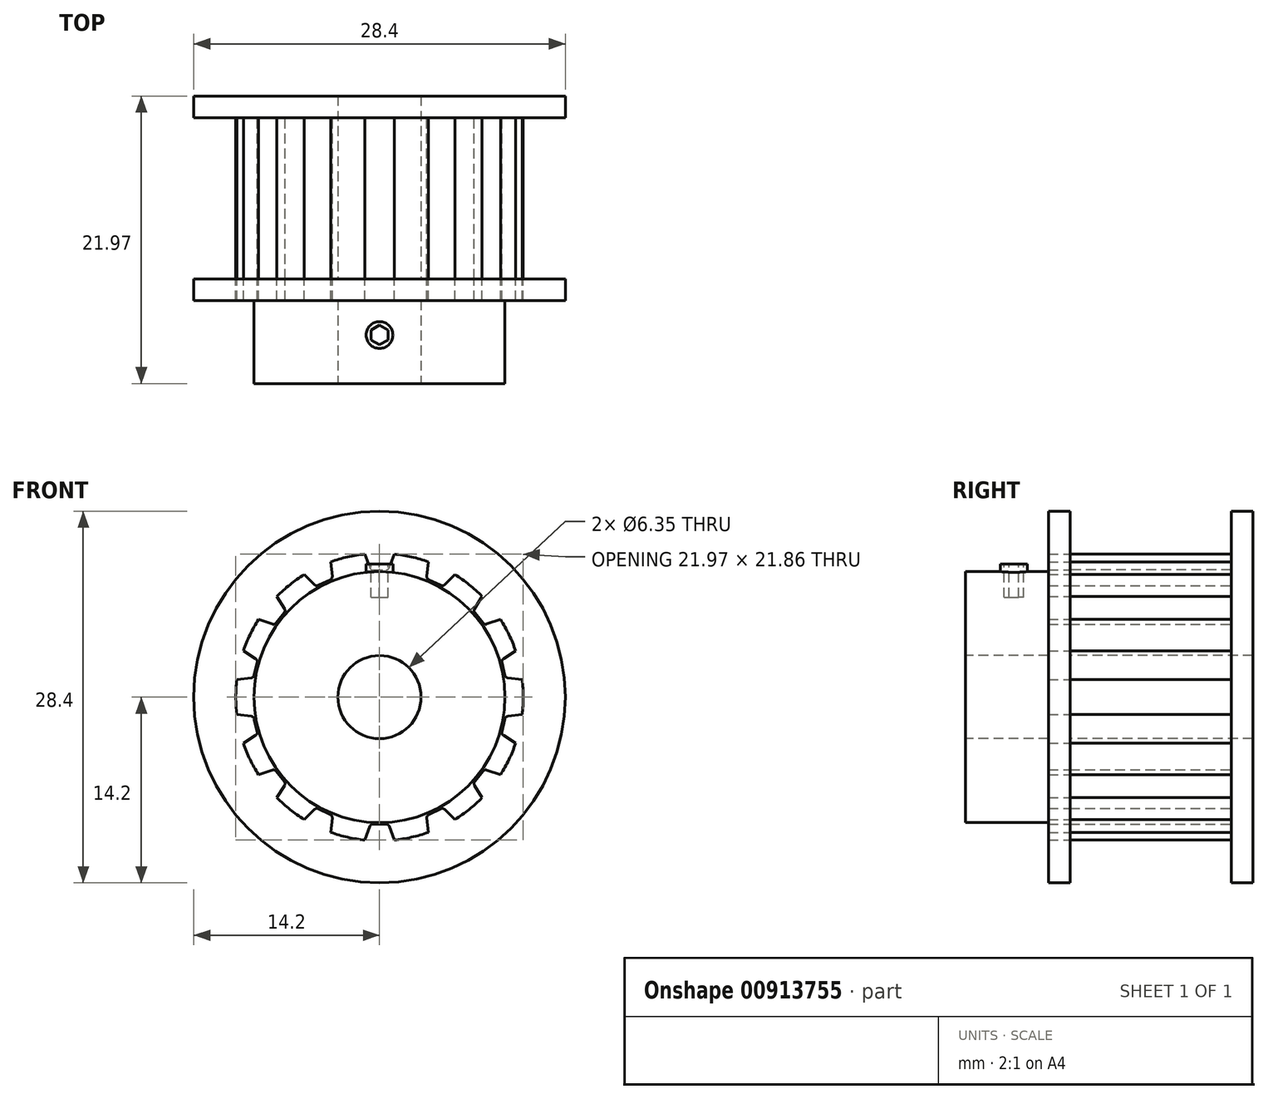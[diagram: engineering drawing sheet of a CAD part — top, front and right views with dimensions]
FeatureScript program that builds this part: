
annotation { "Feature Type Name" : "Feature", "Feature Type Description" : "" }
export const myFeature = defineFeature(function(context is Context, id is Id, definition is map)
    precondition{}
    {
        {
            var Q0;
            Q0=qCreatedBy(makeId("Front.planeOp"),FACE);
            var sketch = newSketch(context, id + "F0", { "sketchPlane" : qUnion([Q0])});
            skCircle(sketch, "E0", {"center": v(0, 0) * mm, "radius": 10.99 * mm});
            skSolve(sketch);
        }
        {
            var Q0;
            Q0=qSketchRegion(id+"F0",true);
            extrude(context, id + "F1", {"entities" : qUnion([Q0]), "depth" : 12.32 * mm});
        }
        {
            var Q0;
            Q0=makeQuery(id+"F1.opExtrude","CAP_FACE",FACE,{"disambiguationData":[OSD([sQuery(id+"F0.wireOp",EDGE,"E0")])],"isStart":false});
            var sketch = newSketch(context, id + "F2", { "sketchPlane" : qUnion([Q0])});
            skLineSegment(sketch, "E1", {"start": v(-1.13, 10.93) * mm, "end": v(-0.69, 9.72) * mm});
            skLineSegment(sketch, "E2", {"start": v(-0.69, 9.72) * mm, "end": v(0.69, 9.72) * mm});
            skLineSegment(sketch, "E3", {"start": v(0.69, 9.72) * mm, "end": v(1.13, 10.93) * mm});
            skLineSegment(sketch, "E4", {"start": v(0, 12.07) * mm, "end": v(0, 0) * mm, "construction": true});
            skArc(sketch, "E5", {"start": v(1.13, 10.93) * mm, "mid": v(0, 10.99) * mm, "end": v(-1.13, 10.93) * mm});
            skSolve(sketch);
        }
        {
            var Q0;
            Q0=qSketchRegion(id+"F2",true);
            extrude(context, id + "F3", {"entities" : qUnion([Q0]), "operationType" : NewBodyOperationType.REMOVE, "oppositeDirection" : true, "depth" : 25.4 * mm});
        }
        {
            var Q0;
            Q0=makeQuery(id+"F3.boolean.opBoolean","COPY",EDGE,{"derivedFrom":makeQuery(id+"F3.opExtrude","SWEPT_EDGE",EDGE,{"disambiguationData":[OSD([sQuery(id+"F0.wireOp",EDGE,"E0"),sQuery(id+"F2.wireOp",EDGE,"E1"),sQuery(id+"F2.wireOp",EDGE,"E5")])]})});
            var Q1;
            Q1=makeQuery(id+"F3.boolean.opBoolean","COPY",EDGE,{"derivedFrom":makeQuery(id+"F3.opExtrude","SWEPT_EDGE",EDGE,{"disambiguationData":[OSD([sQuery(id+"F0.wireOp",EDGE,"E0"),sQuery(id+"F2.wireOp",EDGE,"E3"),sQuery(id+"F2.wireOp",EDGE,"E5")])]})});
            var Q2;
            Q2=makeQuery(id+"F3.boolean.opBoolean","COPY",EDGE,{"derivedFrom":makeQuery(id+"F3.opExtrude","SWEPT_EDGE",EDGE,{"disambiguationData":[OSD([sQuery(id+"F2.wireOp",EDGE,"E1"),sQuery(id+"F2.wireOp",EDGE,"E2")])]})});
            var Q3;
            Q3=makeQuery(id+"F3.boolean.opBoolean","COPY",EDGE,{"derivedFrom":makeQuery(id+"F3.opExtrude","SWEPT_EDGE",EDGE,{"disambiguationData":[OSD([sQuery(id+"F2.wireOp",EDGE,"E2"),sQuery(id+"F2.wireOp",EDGE,"E3")])]})});
            fillet(context, id + "F4", {"entities" : qUnion([Q0, Q1, Q2, Q3]), "radius" : 0.25 * mm, "tangentPropagation" : true, "allowEdgeOverflow" : false});
        }
        {
            var Q0;
            Q0=qCreatedBy(makeId("Right.planeOp"),FACE);
            var sketch = newSketch(context, id + "F5", { "sketchPlane" : qUnion([Q0])});
            skLineSegment(sketch, "E6", {"start": v(-15.42, 0) * mm, "end": v(11.48, 0) * mm, "construction": true});
            skSolve(sketch);
        }
        {
            var Q0;
            Q0=makeQuery(id+"F3.boolean.opBoolean","COPY",FACE,{"derivedFrom":makeQuery(id+"F3.opExtrude","SWEPT_FACE",FACE,{"disambiguationData":[OSD([sQuery(id+"F2.wireOp",EDGE,"E1")])]})});
            var Q1;
            Q1=makeQuery(id+"F3.boolean.opBoolean","COPY",FACE,{"derivedFrom":makeQuery(id+"F3.opExtrude","SWEPT_FACE",FACE,{"disambiguationData":[OSD([sQuery(id+"F2.wireOp",EDGE,"E2")])]})});
            var Q2;
            Q2=makeQuery(id+"F3.boolean.opBoolean","COPY",FACE,{"derivedFrom":makeQuery(id+"F3.opExtrude","SWEPT_FACE",FACE,{"disambiguationData":[OSD([sQuery(id+"F2.wireOp",EDGE,"E3")])]})});
            var Q3;
            Q3=makeQuery(id+"F4.opFillet","BLEND_FACE",FACE,{"disambiguationData":[OSD([sQuery(id+"F0.wireOp",EDGE,"E0"),sQuery(id+"F2.wireOp",EDGE,"E1"),sQuery(id+"F2.wireOp",EDGE,"E5")])]});
            var Q4;
            Q4=makeQuery(id+"F4.opFillet","BLEND_FACE",FACE,{"disambiguationData":[OSD([sQuery(id+"F2.wireOp",EDGE,"E1"),sQuery(id+"F2.wireOp",EDGE,"E2")])]});
            var Q5;
            Q5=makeQuery(id+"F4.opFillet","BLEND_FACE",FACE,{"disambiguationData":[OSD([sQuery(id+"F2.wireOp",EDGE,"E2"),sQuery(id+"F2.wireOp",EDGE,"E3")])]});
            var Q6;
            Q6=makeQuery(id+"F4.opFillet","BLEND_FACE",FACE,{"disambiguationData":[OSD([sQuery(id+"F0.wireOp",EDGE,"E0"),sQuery(id+"F2.wireOp",EDGE,"E3"),sQuery(id+"F2.wireOp",EDGE,"E5")])]});
            var Q7;
            Q7=sQuery(id+"F5.wireOp",EDGE,"E6");
            circularPattern(context, id + "F6", {"faces" : qUnion([Q0, Q1, Q2, Q3, Q4, Q5, Q6]), "axis" : qUnion([Q7]), "angle" : 25.71 * degree, "instanceCount" : 14, "patternType" : PatternType.FACE});
        }
        {
            var Q0;
            Q0=makeQuery(id+"F1.opExtrude","CAP_FACE",FACE,{"disambiguationData":[OSD([sQuery(id+"F0.wireOp",EDGE,"E0")])],"isStart":false});
            var sketch = newSketch(context, id + "F7", { "sketchPlane" : qUnion([Q0])});
            skCircle(sketch, "E7", {"center": v(0, 0) * mm, "radius": 14.2 * mm});
            skSolve(sketch);
        }
        {
            var Q0;
            Q0=makeQuery(id+"F7.imprint","IMPRINT",FACE,{"disambiguationData":[TD([[makeQuery(id+"F7.imprint","IMPRINT",EDGE,{"derivedFrom":sQuery(id+"F7.wireOp",EDGE,"E7")}),1.0]])]});
            var Q1;
            {var subQ0=sQuery(id+"F2.wireOp",EDGE,"E1");var subQ1=makeQuery(id+"F3.boolean.opBoolean","COPY",EDGE,{"derivedFrom":makeQuery(id+"F3.opExtrude","CAP_EDGE",EDGE,{"disambiguationData":[OSD([subQ0])],"isStart":true})});Q1=makeQuery(id+"F7.imprint","IMPRINT",FACE,{"disambiguationData":[TD([[makeQuery(id+"F7.imprint","IMPRINT",EDGE,{"derivedFrom":subQ1}),-1.0]])]});}
            extrude(context, id + "F8", {"entities" : qUnion([Q0, Q1]), "operationType" : NewBodyOperationType.ADD, "depth" : 1.65 * mm});
        }
        {
            var Q0;
            Q0=qCreatedBy(makeId("Front.planeOp"),FACE);
            var sketch = newSketch(context, id + "F9", { "sketchPlane" : qUnion([Q0])});
            skCircle(sketch, "E8", {"center": v(0, 0) * mm, "radius": 14.2 * mm});
            skSolve(sketch);
        }
        {
            var Q0;
            Q0=qSketchRegion(id+"F9",true);
            extrude(context, id + "F10", {"entities" : qUnion([Q0]), "operationType" : NewBodyOperationType.ADD, "oppositeDirection" : true, "depth" : 1.65 * mm});
        }
        {
            var Q0;
            Q0=makeQuery(id+"F8.opExtrude","CAP_FACE",FACE,{"disambiguationData":[OSD([sQuery(id+"F7.wireOp",EDGE,"E7")])],"isStart":false});
            var sketch = newSketch(context, id + "F11", { "sketchPlane" : qUnion([Q0])});
            skCircle(sketch, "E9", {"center": v(0, 0) * mm, "radius": 9.59 * mm});
            skSolve(sketch);
        }
        {
            var Q0;
            Q0=makeQuery(id+"F11.imprint","IMPRINT",FACE,{"disambiguationData":[TD([[makeQuery(id+"F11.imprint","IMPRINT",EDGE,{"derivedFrom":sQuery(id+"F11.wireOp",EDGE,"E9")}),1.0]])]});
            extrude(context, id + "F12", {"entities" : qUnion([Q0]), "operationType" : NewBodyOperationType.ADD, "depth" : 6.35 * mm});
        }
        {
            var Q0;
            Q0=makeQuery(id+"F12.opExtrude","CAP_FACE",FACE,{"disambiguationData":[OSD([sQuery(id+"F11.wireOp",EDGE,"E9")])],"isStart":false});
            var sketch = newSketch(context, id + "F13", { "sketchPlane" : qUnion([Q0])});
            skCircle(sketch, "E10", {"center": v(0, 0) * mm, "radius": 3.18 * mm});
            skSolve(sketch);
        }
        {
            var Q0;
            Q0=qSketchRegion(id+"F13",true);
            extrude(context, id + "F14", {"entities" : qUnion([Q0]), "operationType" : NewBodyOperationType.REMOVE, "oppositeDirection" : true, "depth" : 25.4 * mm});
        }
        {
            var Q0;
            Q0=qCreatedBy(makeId("Top.planeOp"),FACE);
            cPlane(context, id + "F15", {"entities" : qUnion([Q0]), "cplaneType" : CPlaneType.OFFSET, "offset" : 10.16 * mm, "width" : 152.4 * mm, "height" : 152.4 * mm});
        }
        {
            var Q0;
            Q0=qCreatedBy(id+"F15.planeOp",FACE);
            var sketch = newSketch(context, id + "F16", { "sketchPlane" : qUnion([Q0])});
            skCircle(sketch, "E11", {"center": v(0, -16.6) * mm, "radius": 1.03 * mm});
            skSolve(sketch);
        }
        {
            var Q0;
            Q0=makeQuery(id+"F16.imprint","IMPRINT",FACE,{"disambiguationData":[TD([[makeQuery(id+"F16.imprint","IMPRINT",EDGE,{"derivedFrom":sQuery(id+"F16.wireOp",EDGE,"E11")}),1.0]])]});
            extrude(context, id + "F17", {"entities" : qUnion([Q0]), "operationType" : NewBodyOperationType.ADD, "oppositeDirection" : true, "depth" : 2.54 * mm});
        }
        {
            var Q0;
            Q0=makeQuery(id+"F17.opExtrude","CAP_FACE",FACE,{"disambiguationData":[OSD([sQuery(id+"F16.wireOp",EDGE,"E11")])],"isStart":true});
            var sketch = newSketch(context, id + "F18", { "sketchPlane" : qUnion([Q0])});
            skCircle(sketch, "E12.cCircle", {"center": v(0, -16.6) * mm, "radius": 0.75 * mm, "construction": true});
            skLineSegment(sketch, "E12.0", {"start": v(0, -15.86) * mm, "end": v(0.65, -16.23) * mm});
            skLineSegment(sketch, "E12.1", {"start": v(0.65, -16.23) * mm, "end": v(0.65, -16.98) * mm});
            skLineSegment(sketch, "E12.2", {"start": v(0.65, -16.98) * mm, "end": v(0, -17.35) * mm});
            skLineSegment(sketch, "E12.3", {"start": v(0, -17.35) * mm, "end": v(-0.65, -16.98) * mm});
            skLineSegment(sketch, "E12.4", {"start": v(-0.65, -16.98) * mm, "end": v(-0.65, -16.23) * mm});
            skLineSegment(sketch, "E12.5", {"start": v(-0.65, -16.23) * mm, "end": v(0, -15.86) * mm});
            skSolve(sketch);
        }
        {
            var Q0;
            Q0=qSketchRegion(id+"F18",true);
            extrude(context, id + "F19", {"entities" : qUnion([Q0]), "operationType" : NewBodyOperationType.REMOVE, "oppositeDirection" : true, "depth" : 2.54 * mm});
        }
    });
